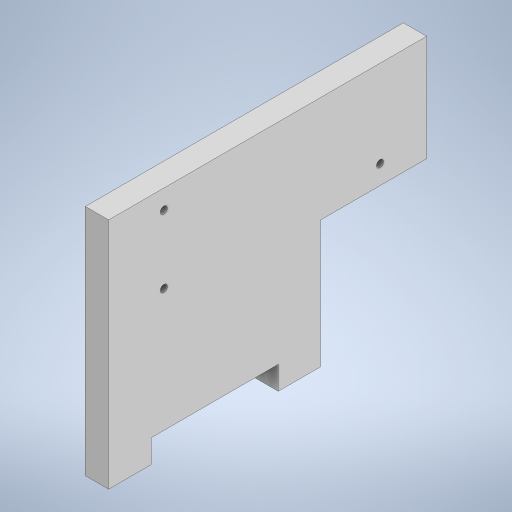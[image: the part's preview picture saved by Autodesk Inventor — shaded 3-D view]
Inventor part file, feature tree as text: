
AUTODESK INVENTOR PART (.ipt)
format: ipt  version: 2024.1 (Build 281209000, 209)  size: 222,720 bytes
history: native  units: mm
features: other x1, extrude x1, sketch x1
ambient origin geometry x8: Origin, YZ Plane, XZ Plane, XY Plane, X Axis, Y Axis, Z Axis, Center Point
bodies: Body1 (feature_tree)
feature tree (3):
  other  "ソリッド1"
  extrude  "押し出し1"  Depth=30.0mm
  sketch  "スケッチ1"
